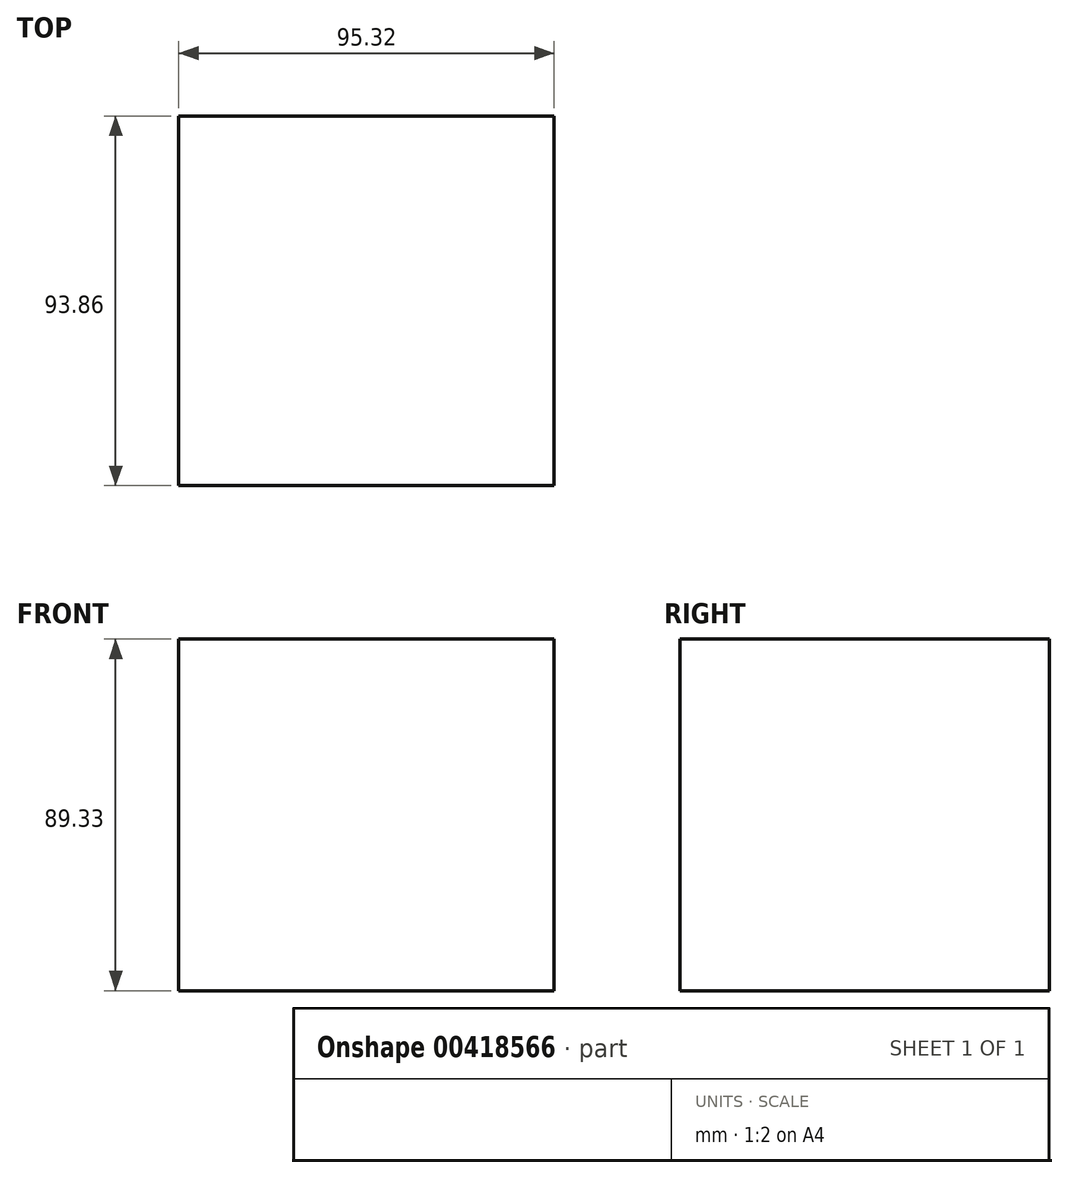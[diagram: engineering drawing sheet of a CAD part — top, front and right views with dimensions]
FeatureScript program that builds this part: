
annotation { "Feature Type Name" : "Feature", "Feature Type Description" : "" }
export const myFeature = defineFeature(function(context is Context, id is Id, definition is map)
    precondition{}
    {
        {
            var Q0;
            Q0=qCreatedBy(makeId("Top.planeOp"),FACE);
            var sketch = newSketch(context, id + "F0", { "sketchPlane" : qUnion([Q0])});
            skLineSegment(sketch, "E0.bottom", {"start": v(47.66, -46.93) * mm, "end": v(-47.66, -46.93) * mm});
            skLineSegment(sketch, "E0.top", {"start": v(47.66, 46.93) * mm, "end": v(-47.66, 46.93) * mm});
            skLineSegment(sketch, "E0.left", {"start": v(47.66, -46.93) * mm, "end": v(47.66, 46.93) * mm});
            skLineSegment(sketch, "E0.right", {"start": v(-47.66, -46.93) * mm, "end": v(-47.66, 46.93) * mm});
            skPoint(sketch, "E0.middle", {"position": v(0, 0) * mm});
            skSolve(sketch);
        }
        {
            var Q0;
            Q0=makeQuery(id+"F0.imprint","IMPRINT",FACE,{"disambiguationData":[TD([[makeQuery(id+"F0.imprint","IMPRINT",EDGE,{"derivedFrom":sQuery(id+"F0.wireOp",EDGE,"E0.bottom")}),-1.0]])]});
            extrude(context, id + "F1", {"entities" : qUnion([Q0]), "depth" : 89.33 * mm});
        }
    });
